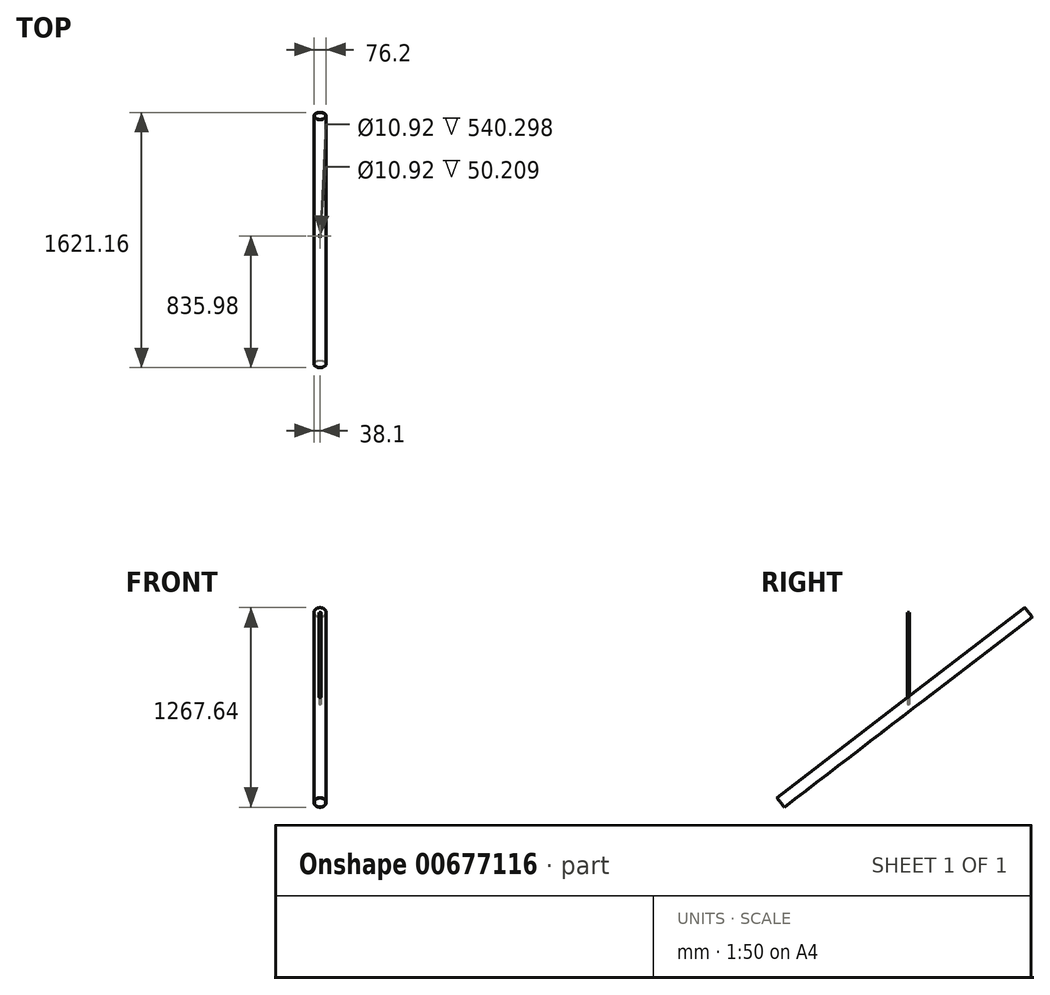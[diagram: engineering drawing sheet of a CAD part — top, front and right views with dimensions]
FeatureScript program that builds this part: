
annotation { "Feature Type Name" : "Feature", "Feature Type Description" : "" }
export const myFeature = defineFeature(function(context is Context, id is Id, definition is map)
    precondition{}
    {
        {
            var Q0;
            Q0=qCreatedBy(makeId("Right.planeOp"),FACE);
            var sketch = newSketch(context, id + "F0", { "sketchPlane" : qUnion([Q0])});
            skLineSegment(sketch, "E0", {"start": v(0, 0) * mm, "end": v(-1574.8, -1207.16) * mm});
            skSolve(sketch);
        }
        {
            var Q0;
            Q0=sQuery(id+"F0.wireOp",VERTEX,"E0.start");
            var Q1;
            Q1=sQuery(id+"F0.wireOp",EDGE,"E0");
            cPlane(context, id + "F1", {"entities" : qUnion([Q0, Q1]), "cplaneType" : CPlaneType.LINE_POINT, "offset" : 25.4 * mm, "width" : 152.4 * mm, "height" : 152.4 * mm});
        }
        {
            var Q0;
            Q0=qCreatedBy(id+"F1.planeOp",FACE);
            var sketch = newSketch(context, id + "F2", { "sketchPlane" : qUnion([Q0])});
            skCircle(sketch, "E1", {"center": v(0, 0) * mm, "radius": 38.1 * mm});
            skCircle(sketch, "E2", {"center": v(0, 0) * mm, "radius": 36.45 * mm});
            skSolve(sketch);
        }
        {
            var Q0;
            Q0=makeQuery(id+"F2.imprint","IMPRINT",FACE,{"disambiguationData":[TD([[makeQuery(id+"F2.imprint","IMPRINT",EDGE,{"derivedFrom":sQuery(id+"F2.wireOp",EDGE,"E1")}),1.0]])]});
            var Q1;
            Q1=sQuery(id+"F0.wireOp",EDGE,"E0");
            sweep(context, id + "F3", {"profiles" : qUnion([Q0]), "path" : qUnion([Q1])});
        }
        {
            var Q0;
            Q0=qCreatedBy(makeId("Right.planeOp"),FACE);
            var sketch = newSketch(context, id + "F4", { "sketchPlane" : qUnion([Q0])});
            skLineSegment(sketch, "E3", {"start": v(0, 0) * mm, "end": v(-762, 0) * mm, "construction": true});
            skLineSegment(sketch, "E4", {"start": v(-762, 0) * mm, "end": v(-762, -584.2) * mm});
            skSolve(sketch);
        }
        {
            var Q0;
            Q0=sQuery(id+"F4.wireOp",VERTEX,"E4.start");
            var Q1;
            Q1=sQuery(id+"F4.wireOp",EDGE,"E4");
            cPlane(context, id + "F5", {"entities" : qUnion([Q0, Q1]), "cplaneType" : CPlaneType.LINE_POINT, "offset" : 25.4 * mm, "width" : 152.4 * mm, "height" : 152.4 * mm});
        }
        {
            var Q0;
            Q0=qCreatedBy(id+"F5.planeOp",FACE);
            var sketch = newSketch(context, id + "F6", { "sketchPlane" : qUnion([Q0])});
            skCircle(sketch, "E5", {"center": v(0, 762) * mm, "radius": 6.35 * mm});
            skCircle(sketch, "E6", {"center": v(0, 762) * mm, "radius": 5.46 * mm});
            skSolve(sketch);
        }
        {
            var Q0;
            Q0=makeQuery(id+"F6.imprint","IMPRINT",FACE,{"disambiguationData":[TD([[makeQuery(id+"F6.imprint","IMPRINT",EDGE,{"derivedFrom":sQuery(id+"F6.wireOp",EDGE,"E5")}),1.0]])]});
            var Q1;
            Q1=sQuery(id+"F4.wireOp",EDGE,"E4");
            sweep(context, id + "F7", {"operationType" : NewBodyOperationType.ADD, "profiles" : qUnion([Q0]), "path" : qUnion([Q1])});
        }
    });
